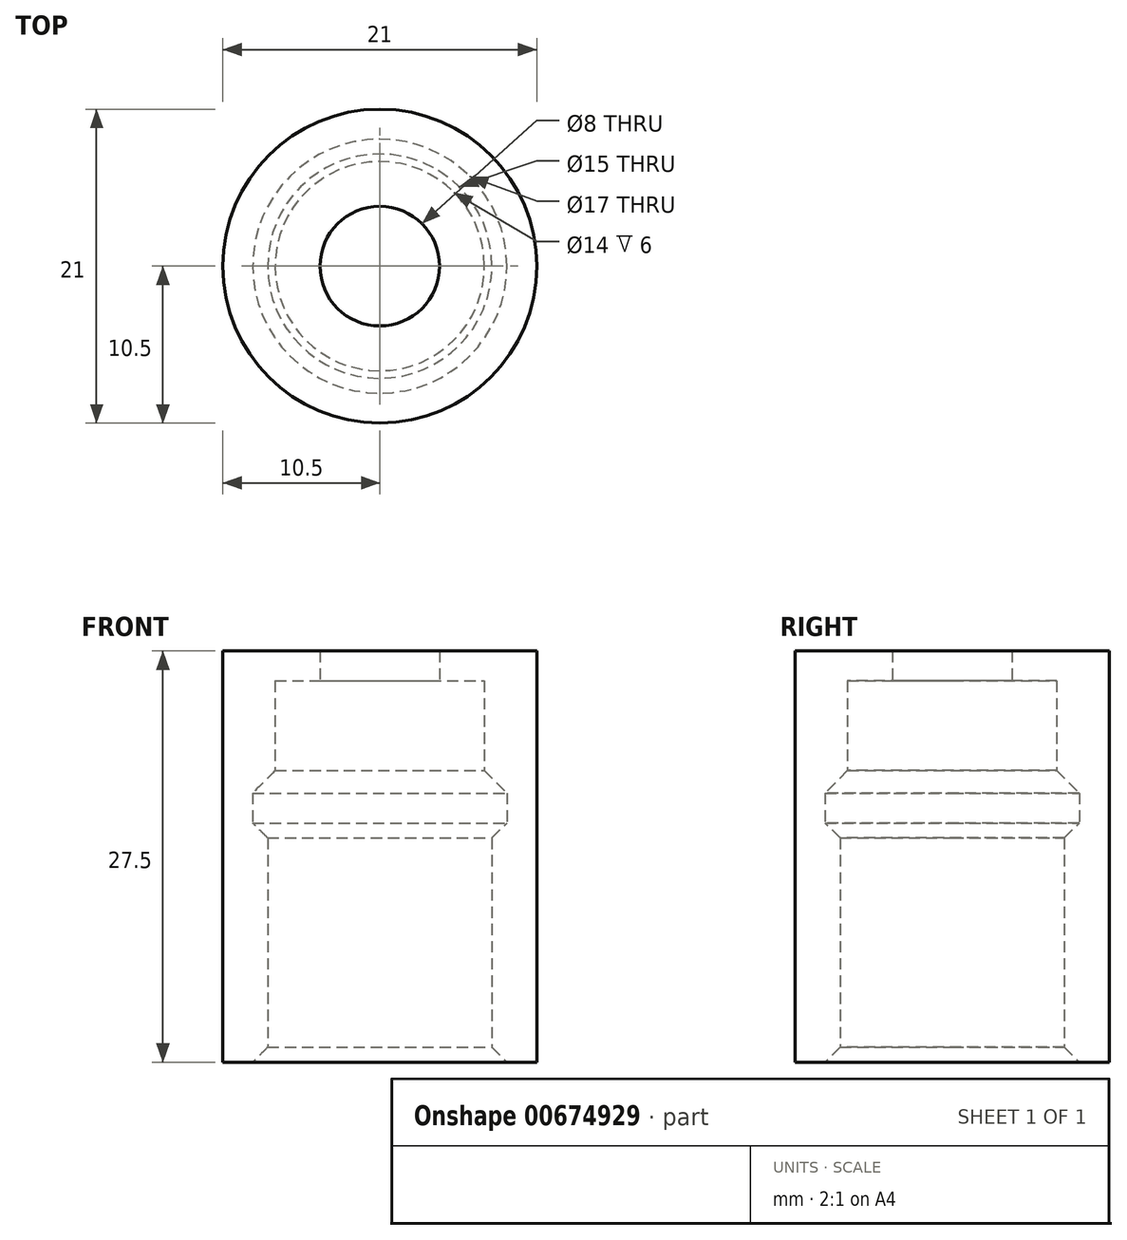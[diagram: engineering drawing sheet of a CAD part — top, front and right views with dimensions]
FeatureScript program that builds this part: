
annotation { "Feature Type Name" : "Feature", "Feature Type Description" : "" }
export const myFeature = defineFeature(function(context is Context, id is Id, definition is map)
    precondition{}
    {
        {
            var Q0;
            Q0=qCreatedBy(makeId("Front.planeOp"),FACE);
            var sketch = newSketch(context, id + "F0", { "sketchPlane" : qUnion([Q0])});
            skLineSegment(sketch, "E0", {"start": v(0, 0) * mm, "end": v(0, 20.2) * mm, "construction": true});
            skLineSegment(sketch, "E1", {"start": v(-4, 27.5) * mm, "end": v(-10.5, 27.5) * mm});
            skLineSegment(sketch, "E2", {"start": v(-8.5, 18) * mm, "end": v(-8.5, 16) * mm});
            skLineSegment(sketch, "E3", {"start": v(-10.5, 0) * mm, "end": v(-10.5, 27.5) * mm});
            skLineSegment(sketch, "E4", {"start": v(-7.5, 15) * mm, "end": v(-7.5, 0) * mm});
            skLineSegment(sketch, "E5", {"start": v(-7.5, 0) * mm, "end": v(-10.5, 0) * mm});
            skLineSegment(sketch, "E6", {"start": v(-8.5, 16) * mm, "end": v(-7.5, 15) * mm});
            skLineSegment(sketch, "E7", {"start": v(-7, 19.5) * mm, "end": v(-7, 25.5) * mm});
            skLineSegment(sketch, "E8", {"start": v(-7, 25.5) * mm, "end": v(-4, 25.5) * mm});
            skLineSegment(sketch, "E9", {"start": v(-4, 27.5) * mm, "end": v(-4, 25.5) * mm});
            skLineSegment(sketch, "E10", {"start": v(-7, 19.5) * mm, "end": v(-8.5, 18) * mm});
            skSolve(sketch);
        }
        {
            var Q0;
            Q0=makeQuery(id+"F0.imprint","IMPRINT",FACE,{"disambiguationData":[TD([[makeQuery(id+"F0.imprint","IMPRINT",EDGE,{"derivedFrom":sQuery(id+"F0.wireOp",EDGE,"E1")}),1.0]])]});
            var Q1;
            Q1=sQuery(id+"F0.wireOp",EDGE,"E0");
            revolve(context, id + "F1", {"entities" : qUnion([Q0]), "axis" : qUnion([Q1]), "revolveType" : RevolveType.FULL});
        }
        {
            var Q0;
            Q0=makeQuery(id+"F1.opRevolve","SWEPT_EDGE",EDGE,{"disambiguationData":[OSD([sQuery(id+"F0.wireOp",EDGE,"E4"),sQuery(id+"F0.wireOp",EDGE,"E5")])]});
            chamfer(context, id + "F2", {"entities" : qUnion([Q0]), "width" : 1 * mm, "tangentPropagation" : true});
        }
    });
